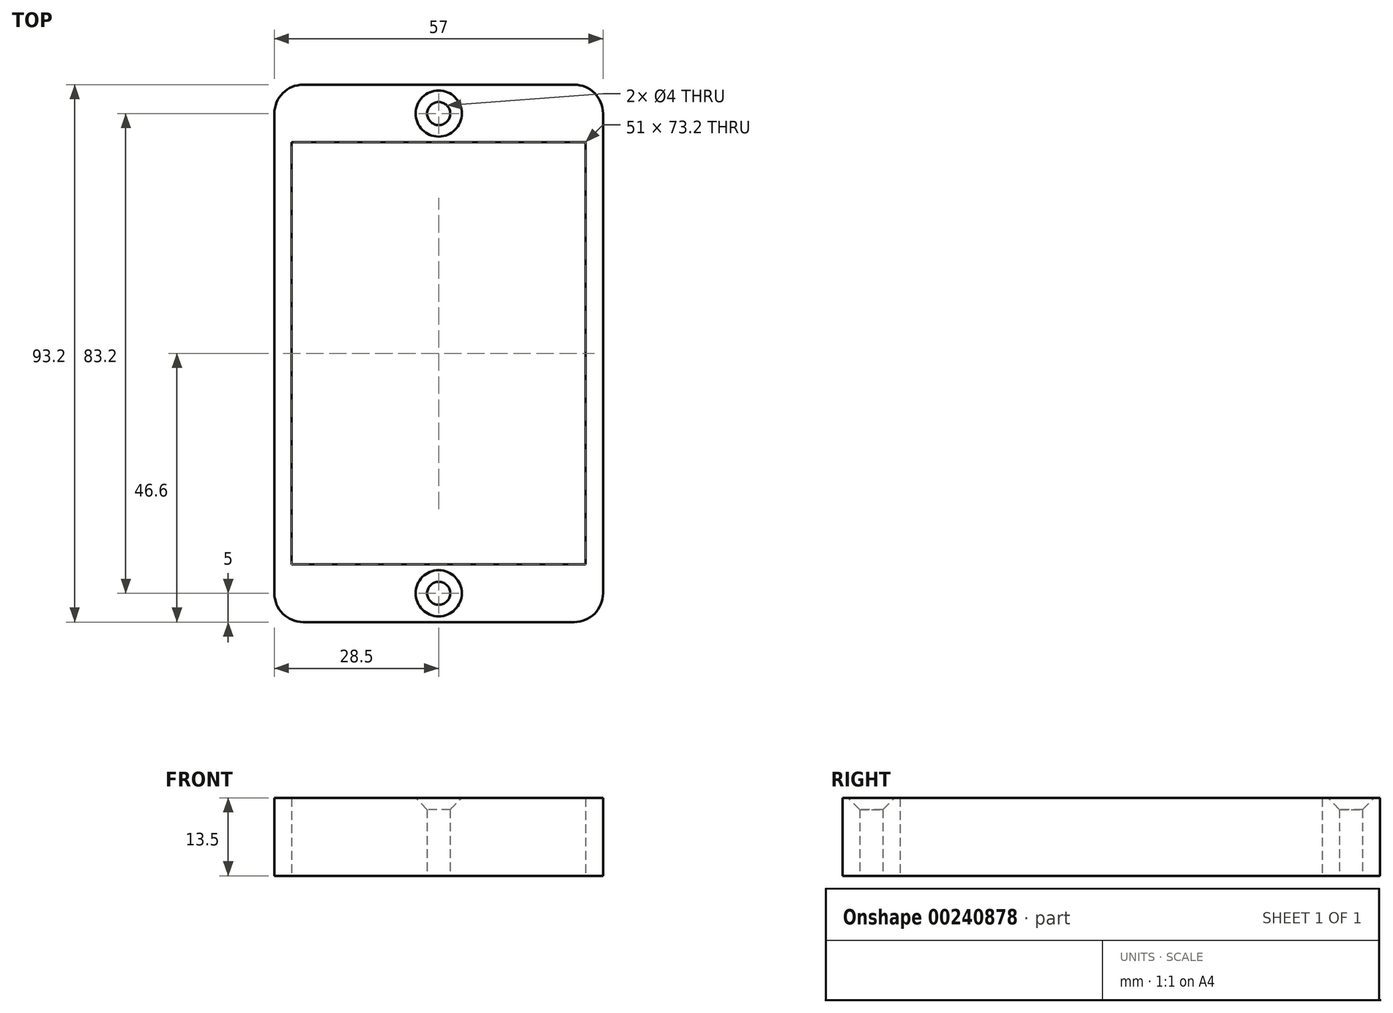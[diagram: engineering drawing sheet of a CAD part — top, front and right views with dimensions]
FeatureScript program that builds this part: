
annotation { "Feature Type Name" : "Feature", "Feature Type Description" : "" }
export const myFeature = defineFeature(function(context is Context, id is Id, definition is map)
    precondition{}
    {
        {
            var Q0;
            Q0=qCreatedBy(makeId("Top.planeOp"),FACE);
            var sketch = newSketch(context, id + "F0", { "sketchPlane" : qUnion([Q0])});
            skLineSegment(sketch, "E0.bottom", {"start": v(25.5, -5) * mm, "end": v(-25.5, -5) * mm});
            skLineSegment(sketch, "E0.top", {"start": v(28.5, 5) * mm, "end": v(-28.5, 5) * mm});
            skLineSegment(sketch, "E0.left", {"start": v(28.5, -5) * mm, "end": v(28.5, 5) * mm});
            skLineSegment(sketch, "E0.right", {"start": v(-28.5, -5) * mm, "end": v(-28.5, 5) * mm});
            skPoint(sketch, "E0.middle", {"position": v(0, 0) * mm});
            skCircle(sketch, "E1", {"center": v(0, 0) * mm, "radius": 2 * mm});
            skLineSegment(sketch, "E2.bottom", {"start": v(28.5, -88.2) * mm, "end": v(-28.5, -88.2) * mm});
            skLineSegment(sketch, "E2.top", {"start": v(25.5, -78.2) * mm, "end": v(-25.5, -78.2) * mm});
            skLineSegment(sketch, "E2.left", {"start": v(28.5, -88.2) * mm, "end": v(28.5, -78.2) * mm});
            skLineSegment(sketch, "E2.right", {"start": v(-28.5, -88.2) * mm, "end": v(-28.5, -78.2) * mm});
            skPoint(sketch, "E2.middle", {"position": v(0, -83.2) * mm});
            skCircle(sketch, "E3", {"center": v(0, -83.2) * mm, "radius": 2 * mm});
            skLineSegment(sketch, "E4.left", {"start": v(-28.5, -5) * mm, "end": v(-28.5, -78.2) * mm});
            skLineSegment(sketch, "E4.right", {"start": v(-25.5, -5) * mm, "end": v(-25.5, -78.2) * mm});
            skLineSegment(sketch, "E5.left", {"start": v(28.5, -5) * mm, "end": v(28.5, -78.2) * mm});
            skLineSegment(sketch, "E5.right", {"start": v(25.5, -5) * mm, "end": v(25.5, -78.2) * mm});
            skSolve(sketch);
        }
        {
            var Q0;
            Q0 = qSketchRegion(id + "F0", true);
            extrude(context, id + "F1", {"entities" : qUnion([Q0]), "depth" : 13.5 * mm});
        }
        {
            var Q0;
            Q0=makeQuery(id+"F1.opExtrude","SWEPT_EDGE",EDGE,{"disambiguationData":[OSD([sQuery(id+"F0.wireOp",EDGE,"E0.top"),sQuery(id+"F0.wireOp",EDGE,"E0.right")])]});
            var Q1;
            Q1=makeQuery(id+"F1.opExtrude","SWEPT_EDGE",EDGE,{"disambiguationData":[OSD([sQuery(id+"F0.wireOp",EDGE,"E0.top"),sQuery(id+"F0.wireOp",EDGE,"E0.left")])]});
            var Q2;
            Q2=makeQuery(id+"F1.opExtrude","SWEPT_EDGE",EDGE,{"disambiguationData":[OSD([sQuery(id+"F0.wireOp",EDGE,"E2.bottom"),sQuery(id+"F0.wireOp",EDGE,"E2.right")])]});
            var Q3;
            Q3=makeQuery(id+"F1.opExtrude","SWEPT_EDGE",EDGE,{"disambiguationData":[OSD([sQuery(id+"F0.wireOp",EDGE,"E2.bottom"),sQuery(id+"F0.wireOp",EDGE,"E2.left")])]});
            fillet(context, id + "F2", {"entities" : qUnion([Q0, Q1, Q2, Q3]), "radius" : 5 * mm, "tangentPropagation" : true, "allowEdgeOverflow" : false});
        }
        {
            var Q0;
            Q0=makeQuery(id+"F1.opExtrude","CAP_EDGE",EDGE,{"disambiguationData":[OSD([sQuery(id+"F0.wireOp",EDGE,"E1")])],"isStart":false});
            var Q1;
            Q1=makeQuery(id+"F1.opExtrude","CAP_EDGE",EDGE,{"disambiguationData":[OSD([sQuery(id+"F0.wireOp",EDGE,"E3")])],"isStart":false});
            chamfer(context, id + "F3", {"entities" : qUnion([Q0, Q1]), "width" : 2 * mm, "tangentPropagation" : true});
        }
    });
